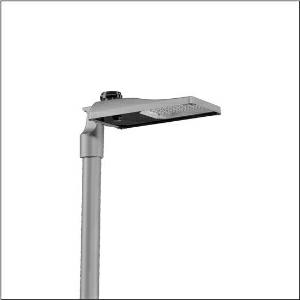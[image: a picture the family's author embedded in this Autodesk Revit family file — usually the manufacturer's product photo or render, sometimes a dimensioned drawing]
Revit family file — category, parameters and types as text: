
# Revit family: streetlight_sl_31_mini___st1_0a_5xh2d3bm08ga_d23b
name_source: partatom
category: Lighting Fixtures
units: mm (PartAtom-declared; Revit-internal decimal feet)

## family parameters
Cut with Voids When Loaded = No
Host = Face
Light Source = No
Part Type = Normal
Room Calculation Point = No
Round Connector Dimension = Use Diameter
Shared = No

## types (1)
- --- (1 x LED, 5880 lm, 39.3 W, 3000K)
    Apparent Load = 39 VA
    CIE Flux Codes = 37 72 97 100 100
    Color Rendering = 70
    Color Temperature = 3000K
    Default Elevation = 1800 mm
    Description = Streetlight SL 31 mini NEMA (7pin) mast luminaire for post-top, side-entry; light control with lens of PMMA; light distribution: ST1.0a, direct asymmetric distribution, for standard-compliant lighting for roads and squares; LED: luminous flux: 5.880lm, light colour: 730, colour temperature: 3000K; luminous efficacy: 149,6lm/W; control: pre-setting: linear dimming characteristic, flexible luminous flux parameterisation, time-dependent luminous flux control, constant luminous flux control, intelligent temperature release in ECG and LED module, overheat protection; luminaire housing, of diecast aluminium, Siteco® metallic grey (DB 702S), corrosivity category C5 high according to DIN EN ISO 12944; cover of toughened safety glass, transparent, mast flange of diecast aluminium, Siteco® metallic grey (DB 702S), spigot size: 76/60mm, mast flange included unmounted; with cable H07RN-F 3x 1.5mm², cable length: 6,5m, connection cable pre-assembled; mains connection: 220..240V, AC, 50/60Hz; power consumption (at start of service life): 39,3W / (at end of service life): 40,7W / (with reduced operation 50%): 18,1W; protection rating (complete): IP66; insulation class (complete): insulation class I (protective earthing); impact resistance: IK09; certification: CE, ENEC, ENEC+, VDE, UKCA; permissible operating ambient temperature for outdoor applications: -40..+50°C; packaging unit: 1 piece

Light Distribution: ST1.0a
    Height = 76 mm
    Lamp = 1 x LED
    Lamp Light Flux = 5880 lm
    Lamp Power = 39.3 W
    Lamp count = 1
    Length = 547 mm
    Luminous efficacy = 150 lm/W
    Manufacturer = Siteco
    ModVariant = No
    Model = 5XH2D3BM08GA
    Number of Poles = 1
    OnlyDefault = Yes
    Power Factor = 1
    Product Name = Streetlight SL 31 mini | ST1.0a
    Product group = mast luminaire | pylon top
    ProductGroupID = 6100
    Protection Class = Protection class I
    Protection Degree = IP 66
    RLX_Detail_Level = 1
    RLX_Emergency_Light_Flux = 0 lm
    RLX_Emergency_Type = 0
    RLX_Emergency_Type_DB = No
    RlxData = <blob elided: 40169 chars, md5=244d3022>
    Socket = socket
    Standby Power = 0 W
    System Light Flux = 5880 lm
    System Power = 39 W
    Type Comments = factory setting: luminous flux: 100 % | dim-lin: 254 | 798 mA
    Type Image = l_1300324.jpg
    URL = http://relux.com
    VarID = @adj_074819
    Voltage = 0 V
    Weight = 0.00 kg
    Width = 265 mm

## geometry (parser evidence)
native form markers: Blend x4, Sweep x9
no freeform markers — native parametric forms only
